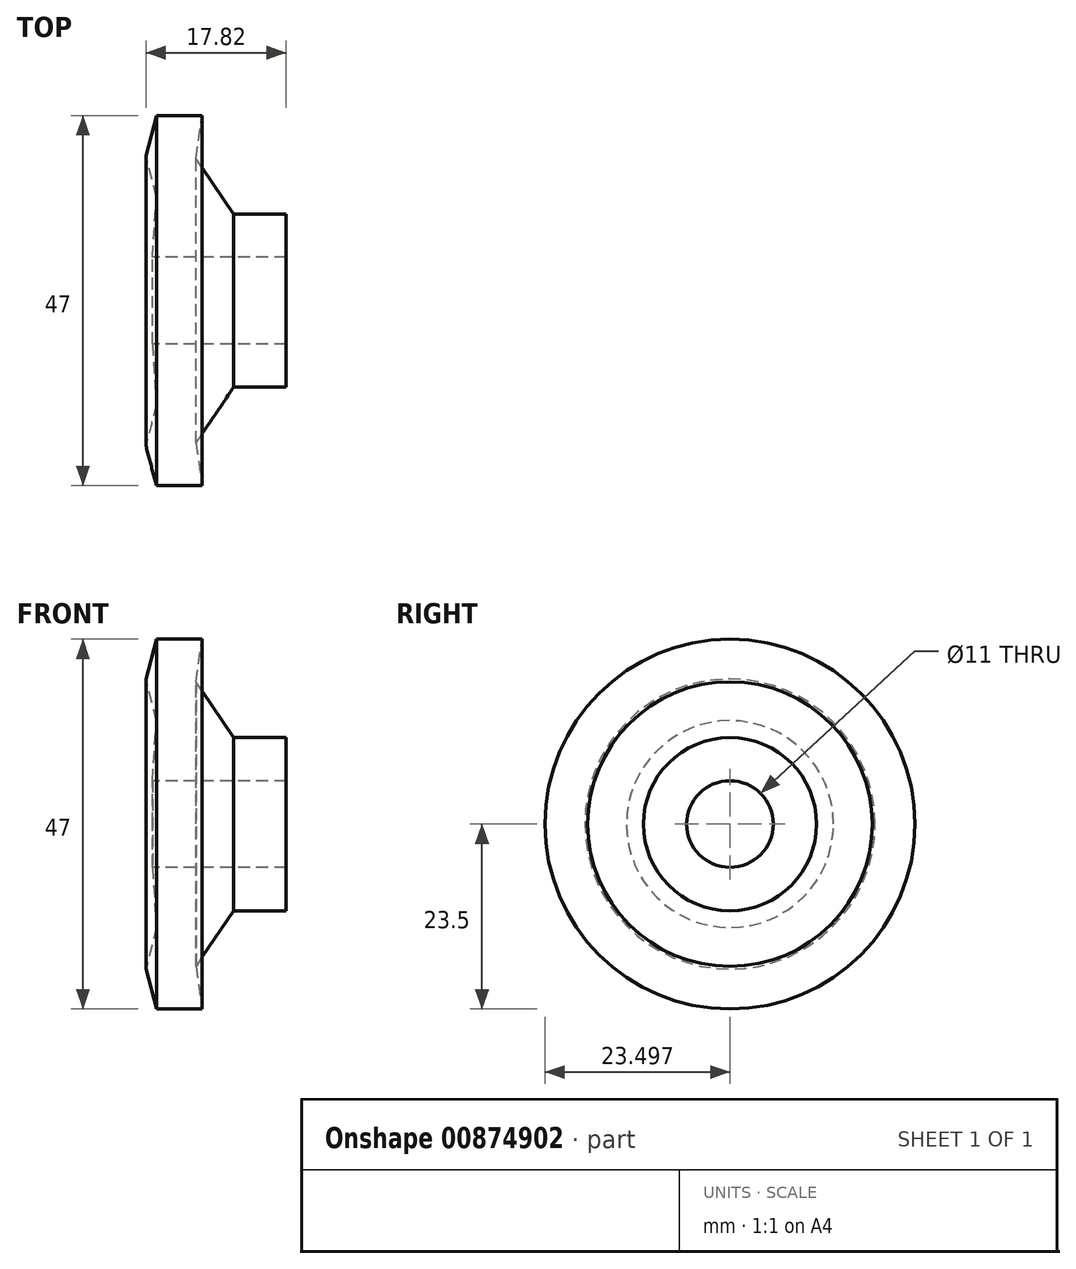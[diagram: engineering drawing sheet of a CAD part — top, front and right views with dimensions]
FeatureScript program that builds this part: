
annotation { "Feature Type Name" : "Feature", "Feature Type Description" : "" }
export const myFeature = defineFeature(function(context is Context, id is Id, definition is map)
    precondition{}
    {
        {
            var Q0;
            Q0=qCreatedBy(makeId("Top.planeOp"),FACE);
            var sketch = newSketch(context, id + "F0", { "sketchPlane" : qUnion([Q0])});
            skLineSegment(sketch, "E0", {"start": v(-18.23, 11.38) * mm, "end": v(-1.23, 11.38) * mm});
            skLineSegment(sketch, "E1", {"start": v(-1.23, 11.38) * mm, "end": v(-1.23, 16.88) * mm});
            skLineSegment(sketch, "E2", {"start": v(-1.23, 16.88) * mm, "end": v(-7.9, 16.88) * mm});
            skLineSegment(sketch, "E3", {"start": v(-7.9, 16.88) * mm, "end": v(-12.7, 23.95) * mm});
            skLineSegment(sketch, "E4", {"start": v(-12.7, 23.95) * mm, "end": v(-11.9, 29.38) * mm});
            skLineSegment(sketch, "E5", {"start": v(-11.9, 29.38) * mm, "end": v(-17.71, 29.38) * mm});
            skLineSegment(sketch, "E6", {"start": v(-27.22, 5.88) * mm, "end": v(0, 5.88) * mm});
            skLineSegment(sketch, "E7", {"start": v(-17.71, 29.38) * mm, "end": v(-19.05, 24.3) * mm});
            skLineSegment(sketch, "E8", {"start": v(-19.05, 24.3) * mm, "end": v(-17.71, 19.02) * mm});
            skLineSegment(sketch, "E9", {"start": v(-17.71, 19.02) * mm, "end": v(-18.23, 11.38) * mm});
            skSolve(sketch);
        }
        {
            var Q0;
            Q0 = qSketchRegion(id + "F0", true);
            var Q1;
            Q1=sQuery(id+"F0.wireOp",EDGE,"E6");
            revolve(context, id + "F1", {"surfaceOperationType" : NewSurfaceOperationType.NEW, "entities" : qUnion([Q0]), "axis" : qUnion([Q1]), "revolveType" : RevolveType.FULL});
        }
    });
